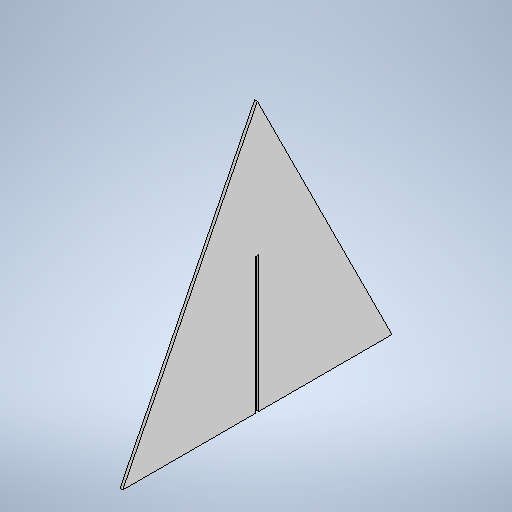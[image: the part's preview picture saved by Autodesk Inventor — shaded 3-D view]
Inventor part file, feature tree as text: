
AUTODESK INVENTOR PART (.ipt)
format: ipt  version: 2025 (Build 290162010, 162A)  size: 249,344 bytes
history: native  units: mm
features: sketch x2, sheet_metal_op x1, extrude x1, other x1
ambient origin geometry x8: Origin, YZ Plane, XZ Plane, XY Plane, X Axis, Y Axis, Z Axis, Center Point
bodies: Solid1 (feature_tree)
feature tree (5):
  sheet_metal_op  "Face1"
  extrude  "Extrusion2"  Depth=300.0mm
  sketch  "Sketch1"  dims[d0=300.0mm d1=300.0mm]
  other  "Plate1"
  sketch  "Sketch3"  dims[d2=3.0mm d7=3.2mm d8=151.0mm d9=0.0mm d10=0.0mm]
